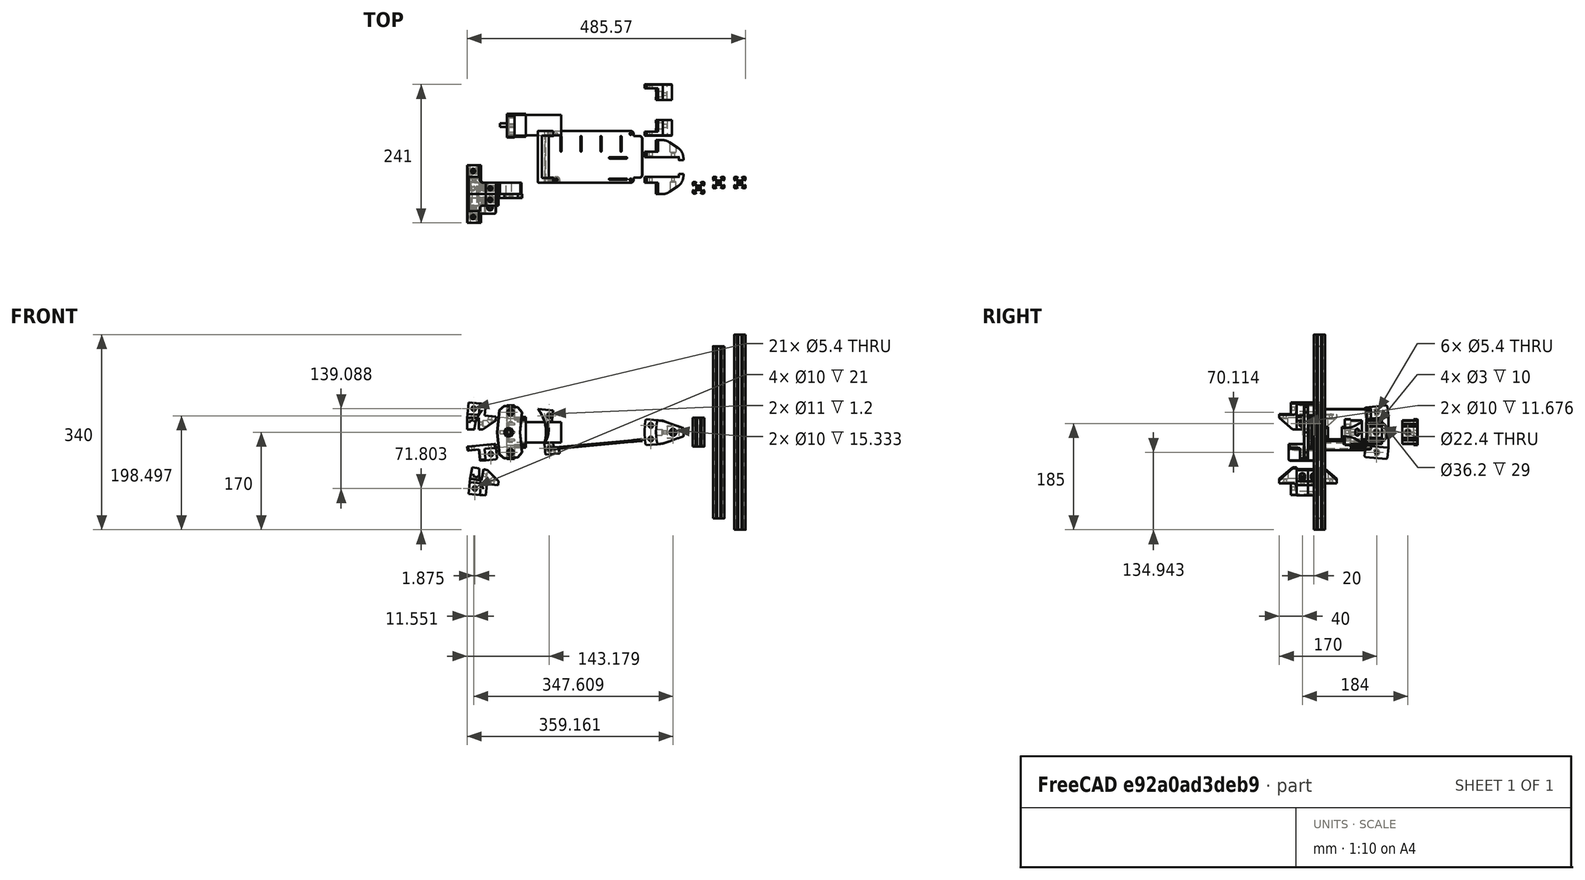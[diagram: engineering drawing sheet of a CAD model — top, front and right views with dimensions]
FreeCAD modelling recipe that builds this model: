
FCSTD DOCUMENT  (FreeCAD 1.2R20260120 (Git shallow))
Label: RC-Robot-parts-export
License: All rights reserved
LicenseURL: https://en.wikipedia.org/wiki/All_rights_reserved
objects: Part::Feature×18, Part::Mirroring×7, App::Part×1, App::Point×1
note: 25 computed .brp shape members not serialized (recipe doc carries the construction recipe); baked Part::Feature solids carry a one-line shape summary decoded from their .brp

FEATURE [Part::Feature] Part__Feature  label="Moteur"
  Placement = pos=(0,100,4e-16) rot=(1,0,0;3.14159rad)
  shape: bbox 107.1 x 35.7 x 35.7 mm, 15 faces (baked)
FEATURE [Part::Feature] Part__Feature001  label="MotorMount2020"
  Placement = pos=(0,100,0) rot=(0,0,1;0rad)
  shape: bbox 33 x 41.69 x 93.42 mm, 38 faces (baked)
FEATURE [Part::Feature] Part__Feature002  label="CoinLateral"
  shape: bbox 49.87 x 50 x 46.78 mm, 44 faces (baked)
FEATURE [Part::Feature] Part__Feature003  label="CoinAvant"
  shape: bbox 67.87 x 35 x 45.07 mm, 39 faces (baked)
FEATURE [Part::Feature] Part__Feature004  label="SupportAxeRoulement"
  shape: bbox 43.29 x 27 x 91.82 mm, 54 faces (baked)
FEATURE [Part::Feature] Part__Feature005  label="CoinInterieurAvant"
  Placement = pos=(0,109,0) rot=(0,0,1;0rad)
  shape: bbox 47.61 x 27 x 45.08 mm, 55 faces (baked)
FEATURE [Part::Feature] Part__Feature006  label="CoinInterieurArriere"
  shape: bbox 52.12 x 27 x 29.69 mm, 26 faces (baked)
FEATURE [Part::Feature] Part__Feature007  label="EquerrePlateauElec"
  shape: bbox 26.68 x 10 x 21.23 mm, 24 faces (baked)
FEATURE [Part::Feature] Part__Feature008  label="PlateauElec001"
  shape: bbox 169.5 x 90 x 18.92 mm, 62 faces (baked)
FEATURE [Part::Feature] Part__Feature009  label="GardeBoue"
  shape: bbox 26.6 x 90 x 59.82 mm, 54 faces (baked)
FEATURE [Part::Feature] Part__Feature010  label="2020-50mm"
  Placement = pos=(0,-9,0) rot=(0,0,1;0rad)
  shape: bbox 20 x 20 x 50 mm, 51 faces (baked)
FEATURE [Part::Feature] Part__Feature011  label="2020-300mm"
  shape: bbox 20 x 20 x 300 mm, 51 faces (baked)
FEATURE [Part::Feature] Part__Feature012  label="2020-340mm"
  shape: bbox 20 x 20 x 340 mm, 51 faces (baked)
FEATURE [Part::Mirroring] Part__Mirroring  label="CoinAvant (Mirror #1)"
  Base = (273.69,10,18.0708)
  MirrorPlane = -> Part__Feature003 [Face1]
  Normal = (0,1,2e-16)
  Placement = pos=(0,34,0) rot=(0,0,1;0rad)
  Source = -> Part__Feature003
FEATURE [Part::Mirroring] Part__Mirroring001  label="CoinInterieurAvant (Mirror #2)"
  Base = (268.379,82,19.5183)
  MirrorPlane = -> Part__Feature005 [Face8]
  Normal = (0,-1,2e-16)
  Placement = pos=(0,89,0) rot=(0,0,1;0rad)
  Source = -> Part__Feature005
FEATURE [Part::Mirroring] Part__Mirroring002  label="CoinInterieurArriere (Mirror #3)"
  Base = (-70.5769,-27,-24.7156)
  MirrorPlane = -> Part__Feature006 [Face12]
  Normal = (-5e-16,-1,3e-16)
  Source = -> Part__Feature006
FEATURE [Part::Mirroring] Part__Mirroring003  label="CoinLateral (Mirror #4)"
  Base = (-45.1472,-5e-15,49.4406)
  MirrorPlane = -> Part__Feature002 [Face9]
  Normal = (0.0937419,5.2e-15,0.995597)
  Placement = pos=(0,0,-159) rot=(0,0,1;0rad)
  Source = -> Part__Feature002
FEATURE [Part::Mirroring] Part__Mirroring004  label="CoinLateralHG"
  Base = (-71.9119,-20,31.8722)
  MirrorPlane = -> Part__Feature002 [Face11]
  Normal = (0,1,2e-16)
  Source = -> Part__Feature002
FEATURE [Part::Mirroring] Part__Mirroring005  label="CoinLateralBG"
  Base = (-68.1623,-20,-87.3039)
  MirrorPlane = -> Part__Mirroring003 [Face11]
  Normal = (-1e-15,1,-1.06e-14)
  Source = -> Part__Mirroring003
FEATURE [Part::Feature] Part__Feature013  label="CoinLateralHD"
  shape: bbox 49.87 x 50 x 46.78 mm, 44 faces (baked)
FEATURE [Part::Feature] Part__Feature014  label="CoinLateral001"
  shape: bbox 49.87 x 50 x 46.78 mm, 44 faces (baked)
FEATURE [Part::Mirroring] Part__Mirroring006  label="CoinLateralBD"
  Base = (-45.1472,-5e-15,49.4406)
  MirrorPlane = -> Part__Feature014 [Face9]
  Normal = (0.0937419,5.2e-15,0.995597)
  Placement = pos=(0,0,-159) rot=(0,0,1;0rad)
  Source = -> Part__Feature014
FEATURE [Part::Feature] Part__Feature015  label="CoinAvant001"
  shape: bbox 67.87 x 35 x 45.07 mm, 39 faces (baked)
FEATURE [Part::Feature] Part__Feature016  label="CoinInterieurArriere001"
  shape: bbox 52.12 x 27 x 29.69 mm, 26 faces (baked)
FEATURE [Part::Feature] Part__Feature017  label="CoinInterieurAvant001"
  Placement = pos=(0,109,0) rot=(0,0,1;0rad)
  shape: bbox 47.61 x 27 x 45.08 mm, 55 faces (baked)
FEATURE [App::Part] Part  label="motor-mounted"
  Group = -> [Part__Feature001,Part__Feature]
  Origin = -> Origin
FEATURE [App::Point] Origin001  label="Origine"
  Role = Origin
